# Revit family: kawneer-350ir_entrance 02_17196
name_source: partatom
category: Doors
revit_build: Autodesk Revit 2015 (Build: 20140905_0730(x64)
units: mm (PartAtom-declared; Revit-internal decimal feet)

## types (1)
- (2)3'-0"W X 7'-0"H W 1'4 TRANS
    Assembly Code = B2030210
    Description = Standard entrances that provide the extra strength for applications where more stringent code requirements include windborne debris protection.
    Frame Finish = Default
    Function = Interior
    Glazing Finish = Glass
    Height = 7' - 0"
    Horizontal Frame Length = 6' - 0"
    INSET = 0' - 2"
    Manufacturer = Kawneer
    Model = 350 IR WITH IR 501 ENTRANCE FRAMING
    Product data url = https://bimobject.com
    Rough Height = 8' - 4"
    Rough Width = 6' - 5"
    Transom Height = 1' - 4"
    Type Comments = 350 IR DOORS WITH IR 501 ENTRANCE FRAMING Hurricane Resistant (1-5/16" INFILL)
    URL = http://www.kawneer.com
    Wall Closure = By host
    Width = 3' - 0"

## geometry (parser evidence)
native form markers: Sweep x29
no freeform markers — native parametric forms only
